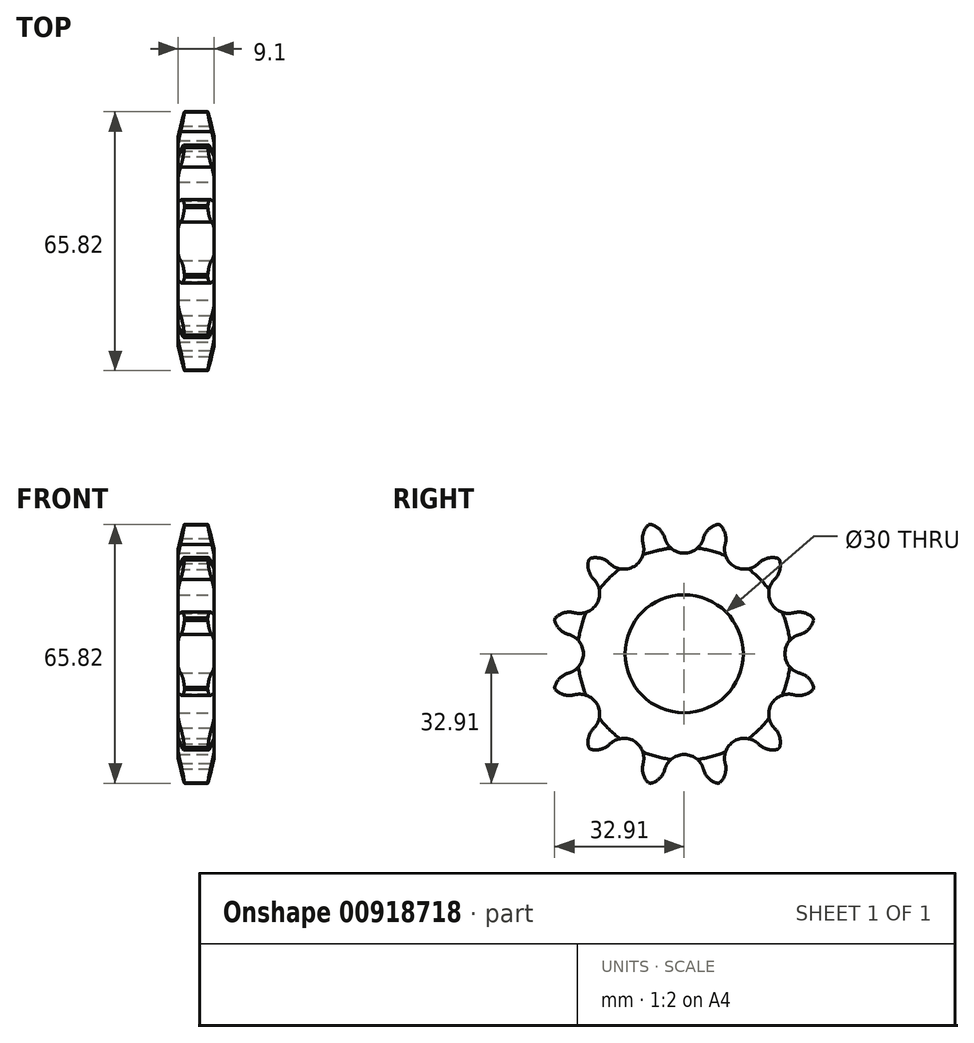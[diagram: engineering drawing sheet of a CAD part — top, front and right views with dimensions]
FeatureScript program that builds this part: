
annotation { "Feature Type Name" : "Feature", "Feature Type Description" : "" }
export const myFeature = defineFeature(function(context is Context, id is Id, definition is map)
    precondition{}
    {
        {
            var Q0;
            Q0=qCreatedBy(makeId("Right.planeOp"),FACE);
            var sketch = newSketch(context, id + "F0", { "sketchPlane" : qUnion([Q0])});
            skArc(sketch, "E0", {"start": v(-23.84, 24.24) * mm, "mid": v(-24.04, 24.04) * mm, "end": v(-24.24, 23.84) * mm});
            skArc(sketch, "E1", {"start": v(-16.34, 21.58) * mm, "mid": v(-19.14, 19.14) * mm, "end": v(-21.58, 16.34) * mm, "construction": true});
            skCircle(sketch, "E2", {"center": v(0, 0) * mm, "radius": 30.67 * mm, "construction": true});
            skLineSegment(sketch, "E3", {"start": v(0, 45.33) * mm, "end": v(0, -43.35) * mm, "construction": true});
            skCircle(sketch, "E4", {"center": v(0, 0) * mm, "radius": 29.7 * mm, "construction": true});
            skLineSegment(sketch, "E5", {"start": v(0, 0) * mm, "end": v(5.78, 30.12) * mm, "construction": true});
            skLineSegment(sketch, "E6", {"start": v(0, 0) * mm, "end": v(10.05, 28.98) * mm, "construction": true});
            skArc(sketch, "E7", {"start": v(8.53, 32.91) * mm, "mid": v(6.21, 31.6) * mm, "end": v(4.9, 29.3) * mm});
            skArc(sketch, "E8.1.0", {"start": v(-9.07, 32.77) * mm, "mid": v(-10.42, 30.48) * mm, "end": v(-10.41, 27.82) * mm});
            skArc(sketch, "E9.trimOffspring", {"start": v(10.41, 27.82) * mm, "mid": v(10.42, 30.48) * mm, "end": v(9.07, 32.77) * mm});
            skArc(sketch, "E10.trimOffspring", {"start": v(-4.9, 29.36) * mm, "mid": v(-0.03, 25.6) * mm, "end": v(4.9, 29.3) * mm});
            skArc(sketch, "E11.trimOffspring", {"start": v(-4.9, 29.3) * mm, "mid": v(-6.21, 31.6) * mm, "end": v(-8.53, 32.91) * mm});
            skArc(sketch, "E12.1.0", {"start": v(-18.93, 22.97) * mm, "mid": v(-12.82, 22.15) * mm, "end": v(-10.41, 27.82) * mm});
            skArc(sketch, "E12.2.0", {"start": v(-27.88, 10.43) * mm, "mid": v(-22.18, 12.77) * mm, "end": v(-22.93, 18.88) * mm});
            skArc(sketch, "E12.3.0", {"start": v(-29.36, -4.9) * mm, "mid": v(-25.6, -0.03) * mm, "end": v(-29.3, 4.9) * mm});
            skArc(sketch, "E12.4.0", {"start": v(-22.97, -18.93) * mm, "mid": v(-22.15, -12.82) * mm, "end": v(-27.82, -10.41) * mm});
            skArc(sketch, "E12.5.0", {"start": v(-10.43, -27.88) * mm, "mid": v(-12.77, -22.18) * mm, "end": v(-18.88, -22.93) * mm});
            skArc(sketch, "E12.6.0", {"start": v(4.9, -29.36) * mm, "mid": v(0.03, -25.6) * mm, "end": v(-4.9, -29.3) * mm});
            skArc(sketch, "E12.7.0", {"start": v(18.93, -22.97) * mm, "mid": v(12.82, -22.15) * mm, "end": v(10.41, -27.82) * mm});
            skArc(sketch, "E12.8.0", {"start": v(27.88, -10.43) * mm, "mid": v(22.18, -12.77) * mm, "end": v(22.93, -18.88) * mm});
            skArc(sketch, "E12.9.0", {"start": v(29.36, 4.9) * mm, "mid": v(25.6, 0.03) * mm, "end": v(29.3, -4.9) * mm});
            skArc(sketch, "E12.10.0", {"start": v(22.97, 18.93) * mm, "mid": v(22.15, 12.82) * mm, "end": v(27.82, 10.41) * mm});
            skArc(sketch, "E12.11.0", {"start": v(10.43, 27.88) * mm, "mid": v(12.77, 22.18) * mm, "end": v(18.88, 22.93) * mm});
            skArc(sketch, "E13.1.0", {"start": v(-9.07, 32.77) * mm, "mid": v(-10.43, 30.48) * mm, "end": v(-10.41, 27.82) * mm});
            skArc(sketch, "E13.2.0", {"start": v(-24.24, 23.84) * mm, "mid": v(-24.27, 21.18) * mm, "end": v(-22.93, 18.88) * mm});
            skArc(sketch, "E13.3.0", {"start": v(-32.91, 8.53) * mm, "mid": v(-31.6, 6.21) * mm, "end": v(-29.3, 4.9) * mm});
            skArc(sketch, "E13.4.0", {"start": v(-32.77, -9.07) * mm, "mid": v(-30.48, -10.43) * mm, "end": v(-27.82, -10.41) * mm});
            skArc(sketch, "E13.5.0", {"start": v(-23.84, -24.24) * mm, "mid": v(-21.18, -24.27) * mm, "end": v(-18.88, -22.93) * mm});
            skArc(sketch, "E13.6.0", {"start": v(-8.53, -32.91) * mm, "mid": v(-6.21, -31.6) * mm, "end": v(-4.9, -29.3) * mm});
            skArc(sketch, "E13.7.0", {"start": v(9.07, -32.77) * mm, "mid": v(10.43, -30.48) * mm, "end": v(10.41, -27.82) * mm});
            skArc(sketch, "E13.8.0", {"start": v(24.24, -23.84) * mm, "mid": v(24.27, -21.18) * mm, "end": v(22.93, -18.88) * mm});
            skArc(sketch, "E13.9.0", {"start": v(32.91, -8.53) * mm, "mid": v(31.6, -6.21) * mm, "end": v(29.3, -4.9) * mm});
            skArc(sketch, "E13.10.0", {"start": v(32.77, 9.07) * mm, "mid": v(30.48, 10.43) * mm, "end": v(27.82, 10.41) * mm});
            skArc(sketch, "E13.11.0", {"start": v(23.84, 24.24) * mm, "mid": v(21.18, 24.27) * mm, "end": v(18.88, 22.93) * mm});
            skArc(sketch, "E14.2.0", {"start": v(-18.88, 22.93) * mm, "mid": v(-21.18, 24.27) * mm, "end": v(-23.84, 24.24) * mm});
            skArc(sketch, "E14.3.0", {"start": v(-27.82, 10.41) * mm, "mid": v(-30.48, 10.42) * mm, "end": v(-32.77, 9.07) * mm});
            skArc(sketch, "E14.4.0", {"start": v(-29.3, -4.9) * mm, "mid": v(-31.6, -6.21) * mm, "end": v(-32.91, -8.53) * mm});
            skArc(sketch, "E14.5.0", {"start": v(-22.93, -18.88) * mm, "mid": v(-24.27, -21.18) * mm, "end": v(-24.24, -23.84) * mm});
            skArc(sketch, "E14.6.0", {"start": v(-10.41, -27.82) * mm, "mid": v(-10.42, -30.48) * mm, "end": v(-9.07, -32.77) * mm});
            skArc(sketch, "E14.7.0", {"start": v(4.9, -29.3) * mm, "mid": v(6.21, -31.6) * mm, "end": v(8.53, -32.91) * mm});
            skArc(sketch, "E14.8.0", {"start": v(18.88, -22.93) * mm, "mid": v(21.18, -24.27) * mm, "end": v(23.84, -24.24) * mm});
            skArc(sketch, "E14.9.0", {"start": v(27.82, -10.41) * mm, "mid": v(30.48, -10.42) * mm, "end": v(32.77, -9.07) * mm});
            skArc(sketch, "E14.10.0", {"start": v(29.3, 4.9) * mm, "mid": v(31.6, 6.21) * mm, "end": v(32.91, 8.53) * mm});
            skArc(sketch, "E14.11.0", {"start": v(22.93, 18.88) * mm, "mid": v(24.27, 21.18) * mm, "end": v(24.24, 23.84) * mm});
            skArc(sketch, "E15.trimOffspring", {"start": v(-32.77, 9.07) * mm, "mid": v(-32.84, 8.8) * mm, "end": v(-32.91, 8.53) * mm});
            skArc(sketch, "E16.trimOffspring", {"start": v(-32.91, -8.53) * mm, "mid": v(-32.84, -8.8) * mm, "end": v(-32.77, -9.07) * mm});
            skArc(sketch, "E17.trimOffspring", {"start": v(-24.24, -23.84) * mm, "mid": v(-24.04, -24.04) * mm, "end": v(-23.84, -24.24) * mm});
            skArc(sketch, "E18.trimOffspring", {"start": v(-9.07, -32.77) * mm, "mid": v(-8.8, -32.84) * mm, "end": v(-8.53, -32.91) * mm});
            skArc(sketch, "E19.trimOffspring", {"start": v(8.53, -32.91) * mm, "mid": v(8.8, -32.84) * mm, "end": v(9.07, -32.77) * mm});
            skArc(sketch, "E20.trimOffspring", {"start": v(23.84, -24.24) * mm, "mid": v(24.04, -24.04) * mm, "end": v(24.24, -23.84) * mm});
            skArc(sketch, "E21.trimOffspring", {"start": v(32.77, -9.07) * mm, "mid": v(32.84, -8.8) * mm, "end": v(32.91, -8.53) * mm});
            skArc(sketch, "E22.trimOffspring", {"start": v(32.91, 8.53) * mm, "mid": v(32.84, 8.8) * mm, "end": v(32.77, 9.07) * mm});
            skArc(sketch, "E23.trimOffspring", {"start": v(24.24, 23.84) * mm, "mid": v(24.04, 24.04) * mm, "end": v(23.84, 24.24) * mm});
            skArc(sketch, "E24.trimOffspring", {"start": v(9.07, 32.77) * mm, "mid": v(8.8, 32.84) * mm, "end": v(8.53, 32.91) * mm});
            skArc(sketch, "E25.trimOffspring", {"start": v(-8.53, 32.91) * mm, "mid": v(-8.8, 32.84) * mm, "end": v(-9.07, 32.77) * mm});
            skArc(sketch, "E26.trimOffspring", {"start": v(-3.36, 26.86) * mm, "mid": v(-7, 26.15) * mm, "end": v(-10.52, 24.94) * mm, "construction": true});
            skArc(sketch, "E27.trimOffspring", {"start": v(10.52, 24.94) * mm, "mid": v(7, 26.15) * mm, "end": v(3.36, 26.86) * mm, "construction": true});
            skArc(sketch, "E28.trimOffspring", {"start": v(21.58, 16.34) * mm, "mid": v(19.14, 19.14) * mm, "end": v(16.34, 21.58) * mm, "construction": true});
            skArc(sketch, "E29.trimOffspring", {"start": v(26.86, 3.36) * mm, "mid": v(26.15, 7) * mm, "end": v(24.94, 10.52) * mm, "construction": true});
            skArc(sketch, "E30.trimOffspring", {"start": v(24.94, -10.52) * mm, "mid": v(26.15, -7) * mm, "end": v(26.86, -3.36) * mm, "construction": true});
            skArc(sketch, "E31.trimOffspring", {"start": v(16.34, -21.58) * mm, "mid": v(19.14, -19.14) * mm, "end": v(21.58, -16.34) * mm, "construction": true});
            skArc(sketch, "E32.trimOffspring", {"start": v(3.36, -26.86) * mm, "mid": v(7, -26.15) * mm, "end": v(10.52, -24.94) * mm, "construction": true});
            skArc(sketch, "E33.trimOffspring", {"start": v(-10.52, -24.94) * mm, "mid": v(-7, -26.15) * mm, "end": v(-3.36, -26.86) * mm, "construction": true});
            skArc(sketch, "E34.trimOffspring", {"start": v(-21.58, -16.34) * mm, "mid": v(-19.14, -19.14) * mm, "end": v(-16.34, -21.58) * mm, "construction": true});
            skArc(sketch, "E35.trimOffspring", {"start": v(-26.86, -3.36) * mm, "mid": v(-26.15, -7) * mm, "end": v(-24.94, -10.52) * mm, "construction": true});
            skArc(sketch, "E36.trimOffspring", {"start": v(-24.94, 10.52) * mm, "mid": v(-26.15, 7) * mm, "end": v(-26.86, 3.36) * mm, "construction": true});
            skCircle(sketch, "E37", {"center": v(0, 0) * mm, "radius": 15 * mm});
            skSolve(sketch);
        }
        {
            var Q0;
            {var subQ12=sQuery(id+"F0.wireOp",EDGE,"E1");Q0=makeQuery(id+"F0.imprint","IMPRINT",FACE,{"disambiguationData":[TD([[makeQuery(id+"F0.imprint","IMPRINT",EDGE,{"derivedFrom":subQ12}),1.0]])]});}
            var Q1;
            {var subQ5=sQuery(id+"F0.wireOp",EDGE,"E13.1.0");Q1=makeQuery(id+"F0.imprint","IMPRINT",FACE,{"disambiguationData":[TD([[makeQuery(id+"F0.imprint","IMPRINT",EDGE,{"derivedFrom":subQ5}),1.0]])]});}
            var Q2;
            {var subQ1=sQuery(id+"F0.wireOp",EDGE,"E7");Q2=makeQuery(id+"F0.imprint","IMPRINT",FACE,{"disambiguationData":[TD([[makeQuery(id+"F0.imprint","IMPRINT",EDGE,{"derivedFrom":subQ1}),1.0]])]});}
            var Q3;
            {var subQ4=sQuery(id+"F0.wireOp",EDGE,"E13.11.0");Q3=makeQuery(id+"F0.imprint","IMPRINT",FACE,{"disambiguationData":[TD([[makeQuery(id+"F0.imprint","IMPRINT",EDGE,{"derivedFrom":subQ4}),1.0]])]});}
            var Q4;
            {var subQ4=sQuery(id+"F0.wireOp",EDGE,"E13.10.0");Q4=makeQuery(id+"F0.imprint","IMPRINT",FACE,{"disambiguationData":[TD([[makeQuery(id+"F0.imprint","IMPRINT",EDGE,{"derivedFrom":subQ4}),1.0]])]});}
            var Q5;
            {var subQ4=sQuery(id+"F0.wireOp",EDGE,"E13.9.0");Q5=makeQuery(id+"F0.imprint","IMPRINT",FACE,{"disambiguationData":[TD([[makeQuery(id+"F0.imprint","IMPRINT",EDGE,{"derivedFrom":subQ4}),1.0]])]});}
            var Q6;
            {var subQ4=sQuery(id+"F0.wireOp",EDGE,"E13.8.0");Q6=makeQuery(id+"F0.imprint","IMPRINT",FACE,{"disambiguationData":[TD([[makeQuery(id+"F0.imprint","IMPRINT",EDGE,{"derivedFrom":subQ4}),1.0]])]});}
            var Q7;
            {var subQ0=sQuery(id+"F0.wireOp",EDGE,"E13.7.0");Q7=makeQuery(id+"F0.imprint","IMPRINT",FACE,{"disambiguationData":[TD([[makeQuery(id+"F0.imprint","IMPRINT",EDGE,{"derivedFrom":subQ0}),1.0]])]});}
            var Q8;
            {var subQ4=sQuery(id+"F0.wireOp",EDGE,"E13.6.0");Q8=makeQuery(id+"F0.imprint","IMPRINT",FACE,{"disambiguationData":[TD([[makeQuery(id+"F0.imprint","IMPRINT",EDGE,{"derivedFrom":subQ4}),1.0]])]});}
            var Q9;
            {var subQ4=sQuery(id+"F0.wireOp",EDGE,"E13.5.0");Q9=makeQuery(id+"F0.imprint","IMPRINT",FACE,{"disambiguationData":[TD([[makeQuery(id+"F0.imprint","IMPRINT",EDGE,{"derivedFrom":subQ4}),1.0]])]});}
            var Q10;
            {var subQ4=sQuery(id+"F0.wireOp",EDGE,"E13.4.0");Q10=makeQuery(id+"F0.imprint","IMPRINT",FACE,{"disambiguationData":[TD([[makeQuery(id+"F0.imprint","IMPRINT",EDGE,{"derivedFrom":subQ4}),1.0]])]});}
            var Q11;
            {var subQ4=sQuery(id+"F0.wireOp",EDGE,"E13.3.0");Q11=makeQuery(id+"F0.imprint","IMPRINT",FACE,{"disambiguationData":[TD([[makeQuery(id+"F0.imprint","IMPRINT",EDGE,{"derivedFrom":subQ4}),1.0]])]});}
            var Q12;
            {var subQ6=sQuery(id+"F0.wireOp",EDGE,"E0");Q12=makeQuery(id+"F0.imprint","IMPRINT",FACE,{"disambiguationData":[TD([[makeQuery(id+"F0.imprint","IMPRINT",EDGE,{"derivedFrom":subQ6}),1.0]])]});}
            extrude(context, id + "F1", {"entities" : qUnion([Q0, Q1, Q2, Q3, Q4, Q5, Q6, Q7, Q8, Q9, Q10, Q11, Q12]), "oppositeDirection" : true, "depth" : 9.1 * mm, "offsetDistance" : 25 * mm, "symmetric" : true});
        }
        {
            var Q0;
            Q0=makeQuery(id+"F1.opExtrude","CAP_EDGE",EDGE,{"disambiguationData":[OSD([sQuery(id+"F0.wireOp",EDGE,"E25.trimOffspring")])],"isStart":true});
            var Q1;
            Q1=makeQuery(id+"F1.opExtrude","CAP_EDGE",EDGE,{"disambiguationData":[OSD([sQuery(id+"F0.wireOp",EDGE,"E0")])],"isStart":true});
            var Q2;
            Q2=makeQuery(id+"F1.opExtrude","CAP_EDGE",EDGE,{"disambiguationData":[OSD([sQuery(id+"F0.wireOp",EDGE,"E15.trimOffspring")])],"isStart":true});
            var Q3;
            Q3=makeQuery(id+"F1.opExtrude","CAP_EDGE",EDGE,{"disambiguationData":[OSD([sQuery(id+"F0.wireOp",EDGE,"E16.trimOffspring")])],"isStart":true});
            var Q4;
            Q4=makeQuery(id+"F1.opExtrude","CAP_EDGE",EDGE,{"disambiguationData":[OSD([sQuery(id+"F0.wireOp",EDGE,"E24.trimOffspring")])],"isStart":true});
            var Q5;
            Q5=makeQuery(id+"F1.opExtrude","CAP_EDGE",EDGE,{"disambiguationData":[OSD([sQuery(id+"F0.wireOp",EDGE,"E23.trimOffspring")])],"isStart":true});
            var Q6;
            Q6=makeQuery(id+"F1.opExtrude","CAP_EDGE",EDGE,{"disambiguationData":[OSD([sQuery(id+"F0.wireOp",EDGE,"E22.trimOffspring")])],"isStart":true});
            var Q7;
            Q7=makeQuery(id+"F1.opExtrude","CAP_EDGE",EDGE,{"disambiguationData":[OSD([sQuery(id+"F0.wireOp",EDGE,"E21.trimOffspring")])],"isStart":true});
            var Q8;
            Q8=makeQuery(id+"F1.opExtrude","CAP_EDGE",EDGE,{"disambiguationData":[OSD([sQuery(id+"F0.wireOp",EDGE,"E20.trimOffspring")])],"isStart":true});
            var Q9;
            Q9=makeQuery(id+"F1.opExtrude","CAP_EDGE",EDGE,{"disambiguationData":[OSD([sQuery(id+"F0.wireOp",EDGE,"E19.trimOffspring")])],"isStart":true});
            var Q10;
            Q10=makeQuery(id+"F1.opExtrude","CAP_EDGE",EDGE,{"disambiguationData":[OSD([sQuery(id+"F0.wireOp",EDGE,"E18.trimOffspring")])],"isStart":true});
            var Q11;
            Q11=makeQuery(id+"F1.opExtrude","CAP_EDGE",EDGE,{"disambiguationData":[OSD([sQuery(id+"F0.wireOp",EDGE,"E17.trimOffspring")])],"isStart":true});
            chamfer(context, id + "F2", {"entities" : qUnion([Q0, Q1, Q2, Q3, Q4, Q5, Q6, Q7, Q8, Q9, Q10, Q11]), "chamferType" : ChamferType.TWO_OFFSETS, "width1" : 6.95 * mm, "oppositeDirection" : false, "width2" : 1.6 * mm, "tangentPropagation" : true});
        }
        {
            var Q0;
            Q0=makeQuery(id+"F1.opExtrude","CAP_EDGE",EDGE,{"disambiguationData":[OSD([sQuery(id+"F0.wireOp",EDGE,"E24.trimOffspring")])],"isStart":false});
            var Q1;
            Q1=makeQuery(id+"F1.opExtrude","CAP_EDGE",EDGE,{"disambiguationData":[OSD([sQuery(id+"F0.wireOp",EDGE,"E25.trimOffspring")])],"isStart":false});
            var Q2;
            Q2=makeQuery(id+"F1.opExtrude","CAP_EDGE",EDGE,{"disambiguationData":[OSD([sQuery(id+"F0.wireOp",EDGE,"E0")])],"isStart":false});
            var Q3;
            Q3=makeQuery(id+"F1.opExtrude","CAP_EDGE",EDGE,{"disambiguationData":[OSD([sQuery(id+"F0.wireOp",EDGE,"E15.trimOffspring")])],"isStart":false});
            var Q4;
            Q4=makeQuery(id+"F1.opExtrude","CAP_EDGE",EDGE,{"disambiguationData":[OSD([sQuery(id+"F0.wireOp",EDGE,"E16.trimOffspring")])],"isStart":false});
            var Q5;
            Q5=makeQuery(id+"F1.opExtrude","CAP_EDGE",EDGE,{"disambiguationData":[OSD([sQuery(id+"F0.wireOp",EDGE,"E23.trimOffspring")])],"isStart":false});
            var Q6;
            Q6=makeQuery(id+"F1.opExtrude","CAP_EDGE",EDGE,{"disambiguationData":[OSD([sQuery(id+"F0.wireOp",EDGE,"E17.trimOffspring")])],"isStart":false});
            var Q7;
            Q7=makeQuery(id+"F1.opExtrude","CAP_EDGE",EDGE,{"disambiguationData":[OSD([sQuery(id+"F0.wireOp",EDGE,"E22.trimOffspring")])],"isStart":false});
            var Q8;
            Q8=makeQuery(id+"F1.opExtrude","CAP_EDGE",EDGE,{"disambiguationData":[OSD([sQuery(id+"F0.wireOp",EDGE,"E21.trimOffspring")])],"isStart":false});
            var Q9;
            Q9=makeQuery(id+"F1.opExtrude","CAP_EDGE",EDGE,{"disambiguationData":[OSD([sQuery(id+"F0.wireOp",EDGE,"E20.trimOffspring")])],"isStart":false});
            var Q10;
            Q10=makeQuery(id+"F1.opExtrude","CAP_EDGE",EDGE,{"disambiguationData":[OSD([sQuery(id+"F0.wireOp",EDGE,"E19.trimOffspring")])],"isStart":false});
            var Q11;
            Q11=makeQuery(id+"F1.opExtrude","CAP_EDGE",EDGE,{"disambiguationData":[OSD([sQuery(id+"F0.wireOp",EDGE,"E18.trimOffspring")])],"isStart":false});
            chamfer(context, id + "F3", {"entities" : qUnion([Q0, Q1, Q2, Q3, Q4, Q5, Q6, Q7, Q8, Q9, Q10, Q11]), "chamferType" : ChamferType.TWO_OFFSETS, "width1" : 1.6 * mm, "oppositeDirection" : false, "width2" : 6.95 * mm, "tangentPropagation" : true});
        }
    });
